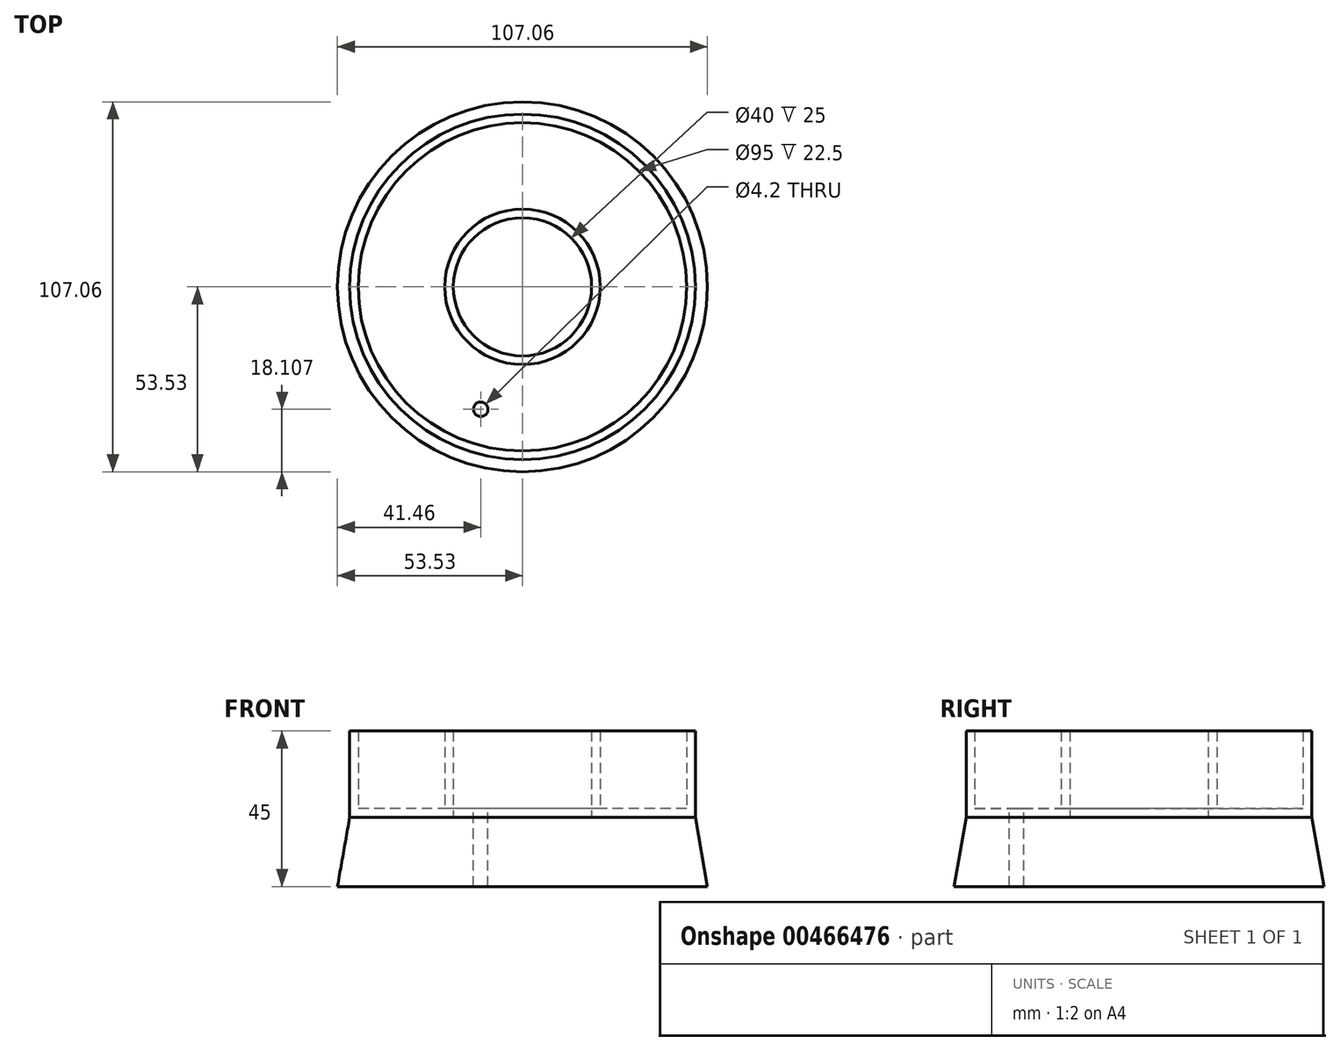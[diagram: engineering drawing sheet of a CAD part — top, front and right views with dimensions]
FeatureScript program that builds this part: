
annotation { "Feature Type Name" : "Feature", "Feature Type Description" : "" }
export const myFeature = defineFeature(function(context is Context, id is Id, definition is map)
    precondition{}
    {
        {
            var Q0;
            Q0=qCreatedBy(makeId("Top.planeOp"),FACE);
            var sketch = newSketch(context, id + "F0", { "sketchPlane" : qUnion([Q0])});
            skCircle(sketch, "E0", {"center": v(0, 0) * mm, "radius": 50 * mm});
            skCircle(sketch, "E1", {"center": v(0, 0) * mm, "radius": 20 * mm});
            skSolve(sketch);
        }
        {
            var Q0;
            Q0=makeQuery(id+"F0.imprint","IMPRINT",FACE,{"disambiguationData":[TD([[makeQuery(id+"F0.imprint","IMPRINT",EDGE,{"derivedFrom":sQuery(id+"F0.wireOp",EDGE,"E0")}),1.0]])]});
            extrude(context, id + "F1", {"entities" : qUnion([Q0]), "depth" : 25 * mm});
        }
        {
            var Q0;
            Q0=makeQuery(id+"F1.opExtrude","CAP_FACE",FACE,{"disambiguationData":[OSD([sQuery(id+"F0.wireOp",EDGE,"E0"),sQuery(id+"F0.wireOp",EDGE,"E1")])],"isStart":false});
            var sketch = newSketch(context, id + "F2", { "sketchPlane" : qUnion([Q0])});
            skPoint(sketch, "E2", {"position": v(-12.07, -35.42) * mm});
            skSolve(sketch);
        }
        {
            var Q0;
            Q0=makeQuery(id+"F1.opExtrude","CAP_FACE",FACE,{"disambiguationData":[OSD([sQuery(id+"F0.wireOp",EDGE,"E0"),sQuery(id+"F0.wireOp",EDGE,"E1")])],"isStart":false});
            shell(context, id + "F3", {"entities" : qUnion([Q0]), "thickness" : 2.5 * mm});
        }
        {
            var Q0;
            Q0=makeQuery(id+"F1.opExtrude","CAP_FACE",FACE,{"disambiguationData":[OSD([sQuery(id+"F0.wireOp",EDGE,"E0"),sQuery(id+"F0.wireOp",EDGE,"E1")])],"isStart":true});
            var sketch = newSketch(context, id + "F4", { "sketchPlane" : qUnion([Q0])});
            skCircle(sketch, "E3.0", {"center": v(0, 0) * mm, "radius": 50 * mm});
            skSolve(sketch);
        }
        {
            var Q0;
            Q0 = qSketchRegion(id + "F4", true);
            extrude(context, id + "F5", {"entities" : qUnion([Q0]), "operationType" : NewBodyOperationType.ADD, "depth" : 20 * mm, "hasDraft" : true, "draftAngle" : 10 * degree});
        }
        {
            var Q0;
            Q0=sQuery(id+"F2.wireOp",VERTEX,"E2");
            var Q1;
            Q1=makeQuery(id+"F1.opExtrude","SWEPT_BODY",BODY,{"disambiguationData":[OSD([sQuery(id+"F0.wireOp",EDGE,"E0"),sQuery(id+"F0.wireOp",EDGE,"E1")])]});
            hole(context, id + "F6", {"style" : HoleStyle.SIMPLE, "endStyle" : HoleEndStyle.THROUGH, "standardTappedOrClearance" : lookupTablePath({ "standard" : "ISO", "engagement" : "75%", "pitch" : "0.8 mm", "size" : "M5", "type" : "Tapped" }), "standardBlindInLast" : lookupTablePath({ "standard" : "ISO", "engagement" : "75%", "pitch" : "0.8 mm", "size" : "M5", "type" : "Tapped" }), "holeDiameter" : 4.2 * mm, "showTappedDepth" : true, "isTappedThrough" : true, "tappedDepth" : 12 * mm, "tapClearance" : 3, "locations" : qUnion([Q0]), "scope" : qUnion([Q1]), "majorDiameter" : 5 * mm});
        }
    });
